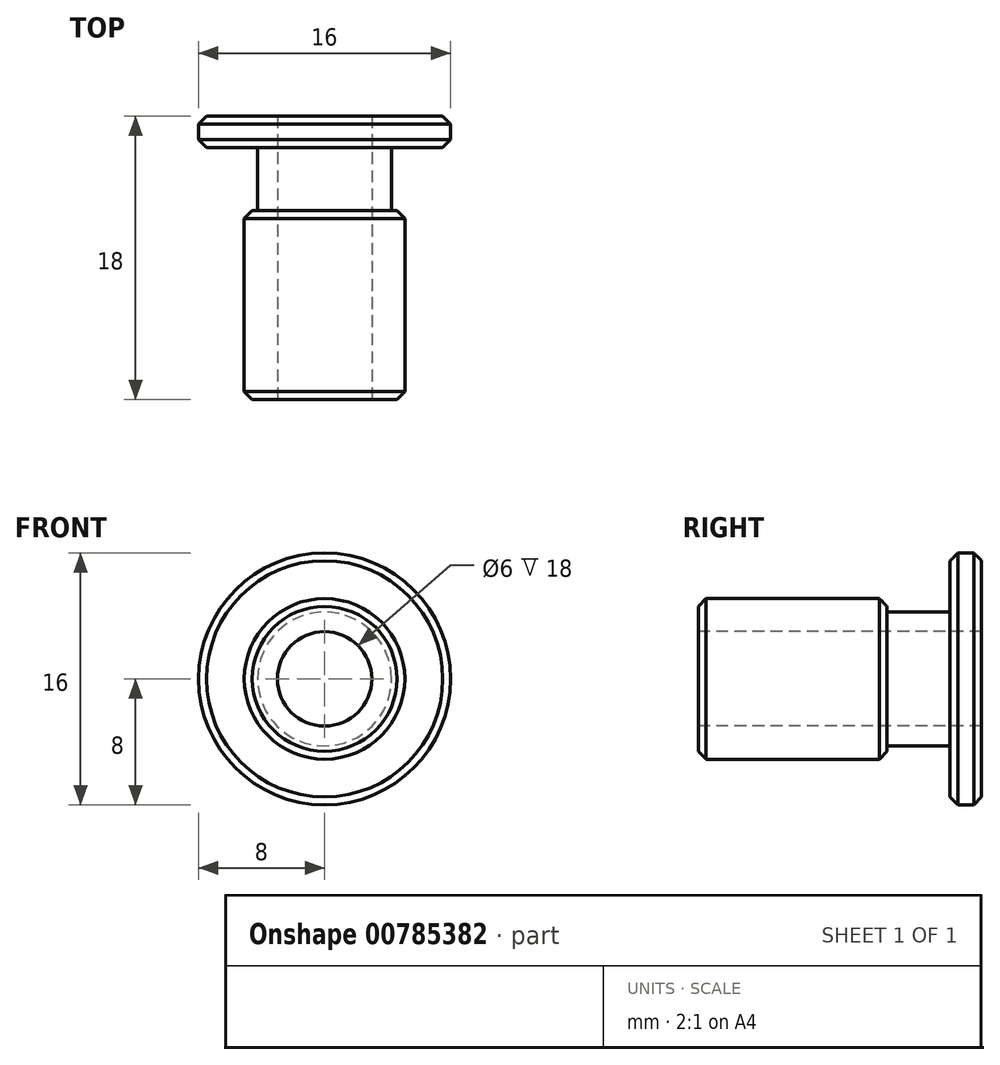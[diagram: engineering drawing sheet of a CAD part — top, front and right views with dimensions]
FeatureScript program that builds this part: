
annotation { "Feature Type Name" : "Feature", "Feature Type Description" : "" }
export const myFeature = defineFeature(function(context is Context, id is Id, definition is map)
    precondition{}
    {
        {
            var Q0;
            Q0=qCreatedBy(makeId("Top.planeOp"),FACE);
            var sketch = newSketch(context, id + "F0", { "sketchPlane" : qUnion([Q0])});
            skLineSegment(sketch, "E0.right", {"start": v(-5.1, 0) * mm, "end": v(-5.1, 12) * mm});
            skLineSegment(sketch, "E1.right", {"start": v(-8, 18) * mm, "end": v(-8, 16) * mm});
            skLineSegment(sketch, "E2", {"start": v(-5.1, 12) * mm, "end": v(-4.25, 12) * mm});
            skLineSegment(sketch, "E3.right", {"start": v(-4.25, 16) * mm, "end": v(-4.25, 12) * mm});
            skLineSegment(sketch, "E4", {"start": v(-8, 16) * mm, "end": v(-4.25, 16) * mm});
            skLineSegment(sketch, "E5", {"start": v(-8, 18) * mm, "end": v(-3, 18) * mm});
            skLineSegment(sketch, "E6.right", {"start": v(-3, 18) * mm, "end": v(-3, 0) * mm});
            skLineSegment(sketch, "E7", {"start": v(-3, 0) * mm, "end": v(-5.1, 0) * mm});
            skLineSegment(sketch, "E8", {"start": v(0, 0) * mm, "end": v(0, 18) * mm, "construction": true});
            skLineSegment(sketch, "E9", {"start": v(0, 0) * mm, "end": v(-9.61, 0) * mm, "construction": true});
            skSolve(sketch);
        }
        {
            var Q0;
            Q0=qSketchRegion(id+"F0",true);
            var Q1;
            Q1=sQuery(id+"F0.wireOp",EDGE,"E8");
            revolve(context, id + "F1", {"entities" : qUnion([Q0]), "axis" : qUnion([Q1]), "revolveType" : RevolveType.FULL});
        }
        {
            var Q0;
            Q0=makeQuery(id+"F1.opRevolve","SWEPT_EDGE",EDGE,{"disambiguationData":[OSD([sQuery(id+"F0.wireOp",EDGE,"E1.right"),sQuery(id+"F0.wireOp",EDGE,"E5")])]});
            var Q1;
            Q1=makeQuery(id+"F1.opRevolve","SWEPT_FACE",FACE,{"disambiguationData":[OSD([sQuery(id+"F0.wireOp",EDGE,"E1.right")])]});
            var Q2;
            Q2=makeQuery(id+"F1.opRevolve","SWEPT_FACE",FACE,{"disambiguationData":[OSD([sQuery(id+"F0.wireOp",EDGE,"E0.right")])]});
            chamfer(context, id + "F2", {"entities" : qUnion([Q0, Q1, Q2]), "width" : .5 * mm, "tangentPropagation" : true});
        }
    });
